# Revit family: QF_True_TBB24-60-2G-Z1-SFT-B-1_Glass_Swing_Door_Back_Bar
name_source: partatom
category: Specialty Equipment
units: mm (PartAtom-declared; Revit-internal decimal feet)

## family parameters
Always vertical = Yes
Cut with Voids When Loaded = No
Part Type = Normal
Room Calculation Point = No
Round Connector Dimension = Use Diameter
Shared = No
Work Plane-Based = No

## types (1)
- QF_True_TBB24-60-2G-Z1-SFT-B-1_Glass_Swing_Door_Back_Bar
    Apparent Power = 0 VA
    Conn Conduit = Yes
    Conn Plug = NEMA 5-15P
    Cycle = 60 Hz
    Default Elevation = 0"
    Depth = 25 11/32"
    Description = Glass Swing Door Back Bar 24" Depth Single Zone Cooler with Stainless Finished Top and Black Exterior
    Elec Conn Connection Height = 0"
    Elec Conn RI Height = 0"
    FL Amps = 3 A
    Foodservice Equipment Identifier = Yes
    HP = 1/4
    Identify Quantity as Lot = Yes
    Length = 60 1/32"
    Manufacturer = True
    Max Overcurrent Protection = 0 A
    Min Ckt Ampacity = 0 A
    Model = TBB24-60-2G-Z1-SFT-B-1
    Number of Poles = 1
    Phase = 1
    Volts = 115 V
    Watts = 368 W
    Weight in Pounds = 345

## geometry (parser evidence)
native form markers: Blend x4, Sweep x25
no freeform markers — native parametric forms only
